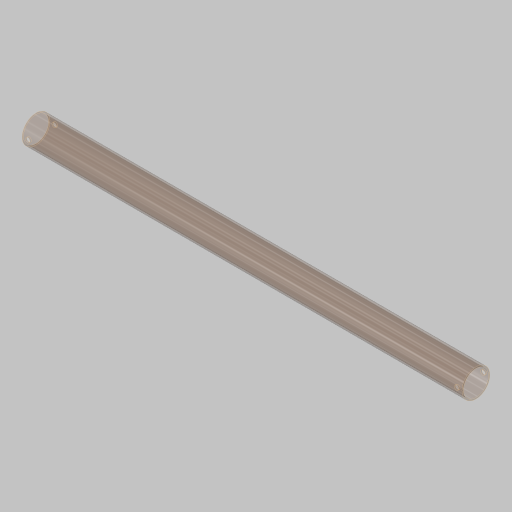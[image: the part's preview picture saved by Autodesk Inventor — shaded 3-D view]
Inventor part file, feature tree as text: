
AUTODESK INVENTOR PART (.ipt)
format: ipt  version: 2023.5 (Build 275446000, 446)  size: 130,048 bytes
history: native  units: in
note: dims shown in document units (in); Inventor stores cm internally (conversion verified against a paired STEP export)
features: sketch x2, extrude x1, plane x1, hole x1
ambient origin geometry x8: Origin, YZ Plane, XZ Plane, XY Plane, X Axis, Y Axis, Z Axis, Center Point
bodies: Solid1 (feature_tree)
feature tree (5):
  extrude  "Extrusion1"  Depth=0.0625in
  plane  "Work Plane1"
  hole  "Hole2"  [1 undecoded]
  sketch  "Sketch1"  dims[d0=1.25in d2=0.0625in]
  sketch  "Sketch3"  dims[d3=19.6875in d4=0.0in d14=0.6875in d15=0.25in d16=0.25in d17=0.201in d18=0.75in d19=0.375in d20=0.25in d21=0.5635in d22=1.0in d23=0.8108in]
note: 1 required parameter value undecoded (feature->parameter linkage not recoverable at this tier; creation-order binding heuristic only, values carry confidence <= 0.55)
